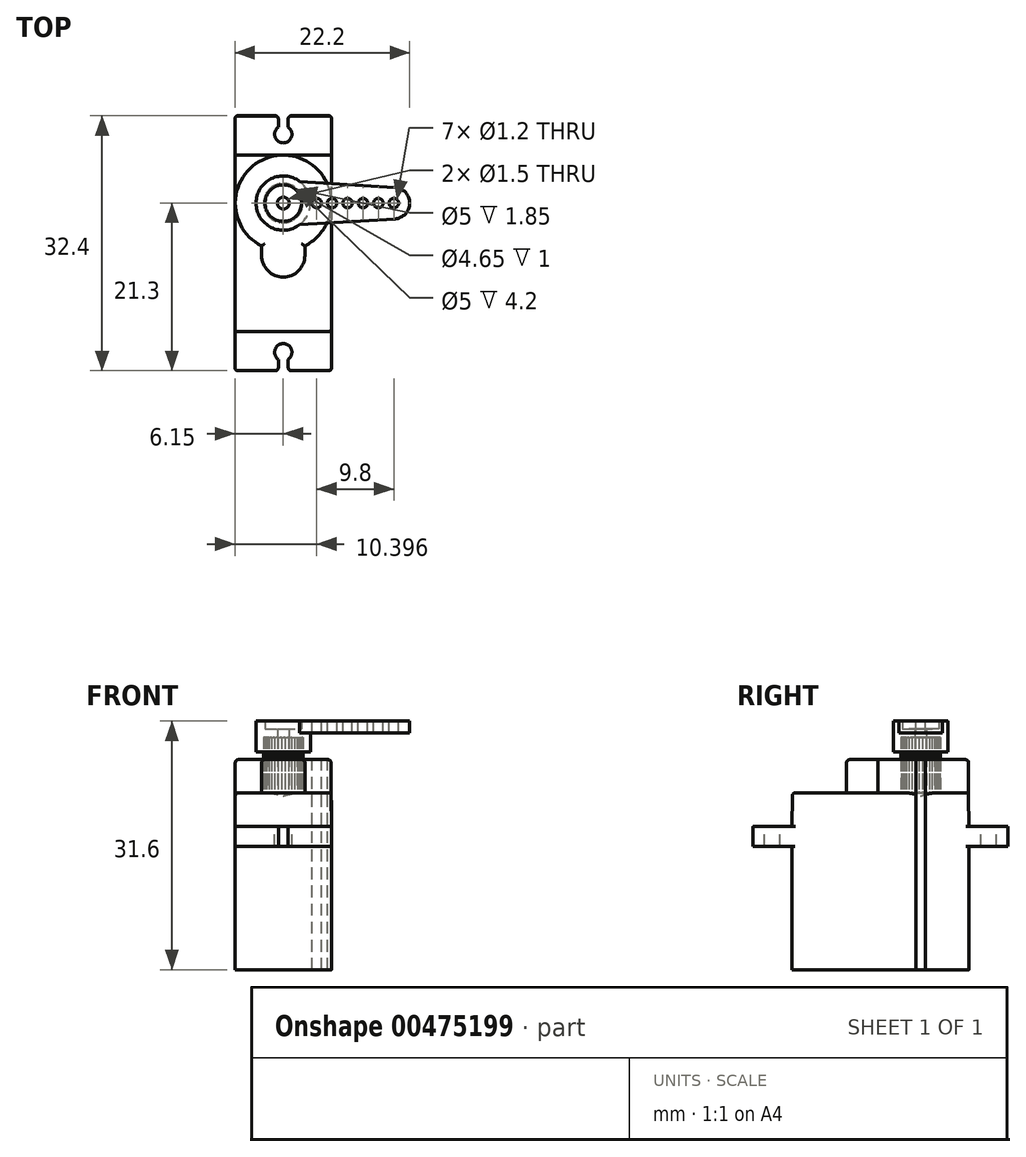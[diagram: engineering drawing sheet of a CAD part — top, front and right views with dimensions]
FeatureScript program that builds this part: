
annotation { "Feature Type Name" : "Feature", "Feature Type Description" : "" }
export const myFeature = defineFeature(function(context is Context, id is Id, definition is map)
    precondition{}
    {
        {
            var Q0;
            Q0=qCreatedBy(makeId("Top.planeOp"),FACE);
            var sketch = newSketch(context, id + "F0", { "sketchPlane" : qUnion([Q0])});
            skLineSegment(sketch, "E0.bottom", {"start": v(6.15, -11.25) * mm, "end": v(-6.15, -11.25) * mm});
            skLineSegment(sketch, "E0.top", {"start": v(6.15, 11.25) * mm, "end": v(-6.15, 11.25) * mm});
            skLineSegment(sketch, "E0.left", {"start": v(6.15, -11.25) * mm, "end": v(6.15, 11.25) * mm});
            skLineSegment(sketch, "E0.right", {"start": v(-6.15, -11.25) * mm, "end": v(-6.15, 11.25) * mm});
            skPoint(sketch, "E0.middle", {"position": v(0, 0) * mm});
            skSolve(sketch);
        }
        {
            var Q0;
            Q0=qSketchRegion(id+"F0",true);
            extrude(context, id + "F1", {"entities" : qUnion([Q0]), "depth" : (22.5 - 15.7) * mm, "hasDraft" : true, "draftAngle" : .5 * degree, "draftPullDirection" : true, "hasSecondDirection" : true, "secondDirectionOppositeDirection" : true, "secondDirectionDepth" : 15.7 * mm});
        }
        {
            var Q0;
            Q0=qCreatedBy(makeId("Top.planeOp"),FACE);
            var sketch = newSketch(context, id + "F2", { "sketchPlane" : qUnion([Q0])});
            skLineSegment(sketch, "E1.bottom", {"start": v(6.15, -16.2) * mm, "end": v(-6.15, -16.2) * mm});
            skLineSegment(sketch, "E1.top", {"start": v(6.15, 16.2) * mm, "end": v(-6.15, 16.2) * mm});
            skLineSegment(sketch, "E1.left", {"start": v(6.15, -16.2) * mm, "end": v(6.15, 16.2) * mm});
            skLineSegment(sketch, "E1.right", {"start": v(-6.15, -16.2) * mm, "end": v(-6.15, 16.2) * mm});
            skPoint(sketch, "E1.middle", {"position": v(0, 0) * mm});
            skSolve(sketch);
        }
        {
            var Q0;
            Q0=qSketchRegion(id+"F2",true);
            extrude(context, id + "F3", {"entities" : qUnion([Q0]), "operationType" : NewBodyOperationType.ADD, "depth" : 2.5 * mm, "hasDraft" : true, "draftAngle" : .5 * degree, "draftPullDirection" : true});
        }
        {
            var Q0;
            {var subQ0=sQuery(id+"F2.wireOp",EDGE,"E1.top");var subQ1=sQuery(id+"F2.wireOp",EDGE,"E1.right");var subQ2=sQuery(id+"F2.wireOp",EDGE,"E1.left");Q0=makeQuery(id+"F3.boolean.opBoolean","SPLIT",FACE,{"disambiguationData":[TD([makeQuery(id+"F1.opExtrude","SWEPT_FACE",FACE,{"disambiguationData":[OSD([sQuery(id+"F0.wireOp",EDGE,"E0.top")])]})])],"derivedFrom":makeQuery(id+"F3.opExtrude","CAP_FACE",FACE,{"disambiguationData":[OSD([sQuery(id+"F2.wireOp",EDGE,"E1.bottom"),subQ0,subQ2,subQ1])],"isStart":false})});}
            var sketch = newSketch(context, id + "F4", { "sketchPlane" : qUnion([Q0])});
            skArc(sketch, "E2", {"start": v(-0.63, 14.76) * mm, "mid": v(0, 12.75) * mm, "end": v(0.63, 14.76) * mm});
            skLineSegment(sketch, "E3", {"start": v(0, 0) * mm, "end": v(0, 13.85) * mm, "construction": true});
            skLineSegment(sketch, "E4", {"start": v(-0.63, 14.76) * mm, "end": v(-0.63, 16.2) * mm});
            skLineSegment(sketch, "E5", {"start": v(-0.62, 16.2) * mm, "end": v(0.62, 16.2) * mm});
            skLineSegment(sketch, "E6", {"start": v(0.62, 16.2) * mm, "end": v(0.62, 14.76) * mm});
            skLineSegment(sketch, "E7", {"start": v(0, 13.85) * mm, "end": v(0, 16.2) * mm, "construction": true});
            skLineSegment(sketch, "E8.MirrorCS", {"start": v(0.62, -16.2) * mm, "end": v(0.62, -14.76) * mm});
            skLineSegment(sketch, "E9.MirrorCS", {"start": v(-0.62, -16.2) * mm, "end": v(0.62, -16.2) * mm});
            skLineSegment(sketch, "E10.MirrorCS", {"start": v(-0.63, -14.76) * mm, "end": v(-0.63, -16.2) * mm});
            skArc(sketch, "E11.MirrorCS", {"start": v(-0.63, -14.76) * mm, "mid": v(0, -12.75) * mm, "end": v(0.63, -14.76) * mm});
            skSolve(sketch);
        }
        {
            var Q0;
            Q0=qSketchRegion(id+"F4",true);
            extrude(context, id + "F5", {"entities" : qUnion([Q0]), "operationType" : NewBodyOperationType.REMOVE, "endBound" : BoundingType.THROUGH_ALL, "oppositeDirection" : true, "depth" : 25 * mm});
        }
        {
            var Q0;
            Q0=makeQuery(id+"F1.*.split.splitOp","SPLIT",EDGE,{"derivedFrom":makeQuery(id+"F1.opExtrude","SWEPT_EDGE",EDGE,{"disambiguationData":[OSD([sQuery(id+"F0.wireOp",EDGE,"E0.bottom"),sQuery(id+"F0.wireOp",EDGE,"E0.left")])]})});
            var Q1;
            Q1=makeQuery(id+"F1.*.split.splitOp","SPLIT",EDGE,{"derivedFrom":makeQuery(id+"F1.opExtrude","SWEPT_EDGE",EDGE,{"disambiguationData":[OSD([sQuery(id+"F0.wireOp",EDGE,"E0.bottom"),sQuery(id+"F0.wireOp",EDGE,"E0.left")])]}),"isFromBackBody":true});
            var Q2;
            Q2=makeQuery(id+"F1.*.split.splitOp","SPLIT",EDGE,{"derivedFrom":makeQuery(id+"F1.opExtrude","SWEPT_EDGE",EDGE,{"disambiguationData":[OSD([sQuery(id+"F0.wireOp",EDGE,"E0.bottom"),sQuery(id+"F0.wireOp",EDGE,"E0.right")])]}),"isFromBackBody":true});
            var Q3;
            Q3=makeQuery(id+"F1.*.split.splitOp","SPLIT",EDGE,{"derivedFrom":makeQuery(id+"F1.opExtrude","SWEPT_EDGE",EDGE,{"disambiguationData":[OSD([sQuery(id+"F0.wireOp",EDGE,"E0.bottom"),sQuery(id+"F0.wireOp",EDGE,"E0.right")])]})});
            var Q4;
            Q4=makeQuery(id+"F1.opExtrude","CAP_FACE",FACE,{"disambiguationData":[OSD([sQuery(id+"F0.wireOp",EDGE,"E0.bottom"),sQuery(id+"F0.wireOp",EDGE,"E0.top"),sQuery(id+"F0.wireOp",EDGE,"E0.left"),sQuery(id+"F0.wireOp",EDGE,"E0.right")])],"isStart":false});
            var Q5;
            Q5=makeQuery(id+"F1.*.split.splitOp","SPLIT",EDGE,{"derivedFrom":makeQuery(id+"F1.opExtrude","SWEPT_EDGE",EDGE,{"disambiguationData":[OSD([sQuery(id+"F0.wireOp",EDGE,"E0.top"),sQuery(id+"F0.wireOp",EDGE,"E0.right")])]})});
            var Q6;
            Q6=makeQuery(id+"F1.*.split.splitOp","SPLIT",EDGE,{"derivedFrom":makeQuery(id+"F1.opExtrude","SWEPT_EDGE",EDGE,{"disambiguationData":[OSD([sQuery(id+"F0.wireOp",EDGE,"E0.top"),sQuery(id+"F0.wireOp",EDGE,"E0.right")])]}),"isFromBackBody":true});
            var Q7;
            Q7=makeQuery(id+"F1.*.split.splitOp","SPLIT",EDGE,{"derivedFrom":makeQuery(id+"F1.opExtrude","SWEPT_EDGE",EDGE,{"disambiguationData":[OSD([sQuery(id+"F0.wireOp",EDGE,"E0.top"),sQuery(id+"F0.wireOp",EDGE,"E0.left")])]}),"isFromBackBody":true});
            var Q8;
            Q8=makeQuery(id+"F1.*.split.splitOp","SPLIT",EDGE,{"derivedFrom":makeQuery(id+"F1.opExtrude","SWEPT_EDGE",EDGE,{"disambiguationData":[OSD([sQuery(id+"F0.wireOp",EDGE,"E0.top"),sQuery(id+"F0.wireOp",EDGE,"E0.left")])]})});
            var Q9;
            Q9=makeQuery(id+"F3.opExtrude","SWEPT_EDGE",EDGE,{"disambiguationData":[OSD([sQuery(id+"F2.wireOp",EDGE,"E1.top"),sQuery(id+"F2.wireOp",EDGE,"E1.left")])]});
            var Q10;
            Q10=makeQuery(id+"F5.boolean.opBoolean","INTERSECT",EDGE,{"derivedFrom":[makeQuery(id+"F3.opExtrude","SWEPT_FACE",FACE,{"disambiguationData":[OSD([sQuery(id+"F2.wireOp",EDGE,"E1.top")])]}),makeQuery(id+"F5.opExtrude","SWEPT_FACE",FACE,{"disambiguationData":[OSD([sQuery(id+"F4.wireOp",EDGE,"E6")])]})]});
            var Q11;
            Q11=makeQuery(id+"F5.boolean.opBoolean","INTERSECT",EDGE,{"derivedFrom":[makeQuery(id+"F3.opExtrude","SWEPT_FACE",FACE,{"disambiguationData":[OSD([sQuery(id+"F2.wireOp",EDGE,"E1.top")])]}),makeQuery(id+"F5.opExtrude","SWEPT_FACE",FACE,{"disambiguationData":[OSD([sQuery(id+"F4.wireOp",EDGE,"E4")])]})]});
            var Q12;
            Q12=makeQuery(id+"F3.opExtrude","SWEPT_EDGE",EDGE,{"disambiguationData":[OSD([sQuery(id+"F2.wireOp",EDGE,"E1.top"),sQuery(id+"F2.wireOp",EDGE,"E1.right")])]});
            var Q13;
            Q13=makeQuery(id+"F3.opExtrude","SWEPT_EDGE",EDGE,{"disambiguationData":[OSD([sQuery(id+"F2.wireOp",EDGE,"E1.bottom"),sQuery(id+"F2.wireOp",EDGE,"E1.right")])]});
            var Q14;
            Q14=makeQuery(id+"F5.boolean.opBoolean","INTERSECT",EDGE,{"derivedFrom":[makeQuery(id+"F3.opExtrude","SWEPT_FACE",FACE,{"disambiguationData":[OSD([sQuery(id+"F2.wireOp",EDGE,"E1.bottom")])]}),makeQuery(id+"F5.opExtrude","SWEPT_FACE",FACE,{"disambiguationData":[OSD([sQuery(id+"F4.wireOp",EDGE,"E10.MirrorCS")])]})]});
            var Q15;
            Q15=makeQuery(id+"F5.boolean.opBoolean","INTERSECT",EDGE,{"derivedFrom":[makeQuery(id+"F3.opExtrude","SWEPT_FACE",FACE,{"disambiguationData":[OSD([sQuery(id+"F2.wireOp",EDGE,"E1.bottom")])]}),makeQuery(id+"F5.opExtrude","SWEPT_FACE",FACE,{"disambiguationData":[OSD([sQuery(id+"F4.wireOp",EDGE,"E8.MirrorCS")])]})]});
            var Q16;
            Q16=makeQuery(id+"F3.opExtrude","SWEPT_EDGE",EDGE,{"disambiguationData":[OSD([sQuery(id+"F2.wireOp",EDGE,"E1.bottom"),sQuery(id+"F2.wireOp",EDGE,"E1.left")])]});
            fillet(context, id + "F6", {"entities" : qUnion([Q0, Q1, Q2, Q3, Q4, Q5, Q6, Q7, Q8, Q9, Q10, Q11, Q12, Q13, Q14, Q15, Q16]), "radius" : .4 * mm, "tangentPropagation" : true, "allowEdgeOverflow" : false});
        }
        {
            var Q0;
            Q0=makeQuery(id+"F1.opExtrude","CAP_FACE",FACE,{"disambiguationData":[OSD([sQuery(id+"F0.wireOp",EDGE,"E0.bottom"),sQuery(id+"F0.wireOp",EDGE,"E0.top"),sQuery(id+"F0.wireOp",EDGE,"E0.left"),sQuery(id+"F0.wireOp",EDGE,"E0.right")])],"isStart":false});
            var sketch = newSketch(context, id + "F7", { "sketchPlane" : qUnion([Q0])});
            skArc(sketch, "E12", {"start": v(2.75, -0.34) * mm, "mid": v(0, 11.2) * mm, "end": v(-2.75, -0.34) * mm});
            skLineSegment(sketch, "E13", {"start": v(-2.75, -0.34) * mm, "end": v(-2.75, -1.56) * mm});
            skLineSegment(sketch, "E14", {"start": v(2.75, -0.34) * mm, "end": v(2.75, -1.56) * mm});
            skArc(sketch, "E15", {"start": v(-2.75, -1.56) * mm, "mid": v(0, -4.3) * mm, "end": v(2.75, -1.56) * mm});
            skCircle(sketch, "E16", {"center": v(0, 5.1) * mm, "radius": 2.5 * mm});
            skSolve(sketch);
        }
        {
            var Q0;
            Q0=qSketchRegion(id+"F7",true);
            extrude(context, id + "F8", {"entities" : qUnion([Q0]), "operationType" : NewBodyOperationType.ADD, "depth" : 4.2 * mm, "hasSecondDirection" : true, "secondDirectionBound" : SecondDirectionBoundingType.UP_TO_NEXT, "secondDirectionOppositeDirection" : true, "secondDirectionDepth" : 25 * mm});
        }
        {
            var Q0;
            Q0=makeQuery(id+"F8.opExtrude","CAP_EDGE",EDGE,{"disambiguationData":[OSD([sQuery(id+"F7.wireOp",EDGE,"E12")])],"isStart":false});
            var Q1;
            Q1=makeQuery(id+"F8.opExtrude","CAP_EDGE",EDGE,{"disambiguationData":[OSD([sQuery(id+"F7.wireOp",EDGE,"E14")])],"isStart":false});
            var Q2;
            Q2=makeQuery(id+"F8.opExtrude","CAP_EDGE",EDGE,{"disambiguationData":[OSD([sQuery(id+"F7.wireOp",EDGE,"E15")])],"isStart":false});
            var Q3;
            Q3=makeQuery(id+"F8.opExtrude","CAP_EDGE",EDGE,{"disambiguationData":[OSD([sQuery(id+"F7.wireOp",EDGE,"E13")])],"isStart":false});
            fillet(context, id + "F9", {"entities" : qUnion([Q0, Q1, Q2, Q3]), "radius" : .4 * mm, "tangentPropagation" : true, "allowEdgeOverflow" : false});
        }
        {
            var Q0;
            Q0=makeQuery(id+"F8.opExtrude","CAP_FACE",FACE,{"disambiguationData":[OSD([sQuery(id+"F7.wireOp",EDGE,"E12"),sQuery(id+"F7.wireOp",EDGE,"E13"),sQuery(id+"F7.wireOp",EDGE,"E14"),sQuery(id+"F7.wireOp",EDGE,"E15"),sQuery(id+"F7.wireOp",EDGE,"E16")])],"isStart":false});
            var sketch = newSketch(context, id + "F10", { "sketchPlane" : qUnion([Q0])});
            skCircle(sketch, "E17", {"center": v(0, 5.1) * mm, "radius": 2.3 * mm, "construction": true});
            skLineSegment(sketch, "E18", {"start": v(-0.23, 7.39) * mm, "end": v(-0.06, 7.57) * mm});
            skLineSegment(sketch, "E19", {"start": v(0.23, 7.39) * mm, "end": v(0.06, 7.57) * mm});
            skArc(sketch, "E20", {"start": v(0.06, 7.57) * mm, "mid": v(0, 7.6) * mm, "end": v(-0.06, 7.57) * mm});
            skLineSegment(sketch, "E21", {"start": v(-0.23, 7.39) * mm, "end": v(0, 5.1) * mm, "construction": true});
            skLineSegment(sketch, "E22", {"start": v(0.23, 7.39) * mm, "end": v(0, 5.1) * mm, "construction": true});
            skLineSegment(sketch, "E23.1.0", {"start": v(-0.67, 7.3) * mm, "end": v(-0.54, 7.51) * mm});
            skArc(sketch, "E23.1.1", {"start": v(-0.42, 7.54) * mm, "mid": v(-0.49, 7.55) * mm, "end": v(-0.54, 7.51) * mm});
            skLineSegment(sketch, "E23.1.2", {"start": v(-0.23, 7.39) * mm, "end": v(-0.42, 7.54) * mm});
            skLineSegment(sketch, "E23.2.0", {"start": v(-1.08, 7.13) * mm, "end": v(-1, 7.36) * mm});
            skArc(sketch, "E23.2.1", {"start": v(-0.9, 7.4) * mm, "mid": v(-0.96, 7.4) * mm, "end": v(-1, 7.36) * mm});
            skLineSegment(sketch, "E23.2.2", {"start": v(-0.67, 7.3) * mm, "end": v(-0.9, 7.4) * mm});
            skLineSegment(sketch, "E23.3.0", {"start": v(-1.46, 6.88) * mm, "end": v(-1.42, 7.12) * mm});
            skArc(sketch, "E23.3.1", {"start": v(-1.32, 7.19) * mm, "mid": v(-1.39, 7.18) * mm, "end": v(-1.42, 7.12) * mm});
            skLineSegment(sketch, "E23.3.2", {"start": v(-1.08, 7.13) * mm, "end": v(-1.32, 7.19) * mm});
            skLineSegment(sketch, "E23.4.0", {"start": v(-1.78, 6.56) * mm, "end": v(-1.8, 6.8) * mm});
            skArc(sketch, "E23.4.1", {"start": v(-1.7, 6.9) * mm, "mid": v(-1.77, 6.87) * mm, "end": v(-1.8, 6.8) * mm});
            skLineSegment(sketch, "E23.4.2", {"start": v(-1.46, 6.88) * mm, "end": v(-1.7, 6.9) * mm});
            skLineSegment(sketch, "E23.5.0", {"start": v(-2.03, 6.18) * mm, "end": v(-2.09, 6.42) * mm});
            skArc(sketch, "E23.5.1", {"start": v(-2.02, 6.52) * mm, "mid": v(-2.08, 6.49) * mm, "end": v(-2.09, 6.42) * mm});
            skLineSegment(sketch, "E23.5.2", {"start": v(-1.78, 6.56) * mm, "end": v(-2.02, 6.52) * mm});
            skLineSegment(sketch, "E23.6.0", {"start": v(-2.2, 5.77) * mm, "end": v(-2.3, 6) * mm});
            skArc(sketch, "E23.6.1", {"start": v(-2.26, 6.1) * mm, "mid": v(-2.3, 6.06) * mm, "end": v(-2.3, 6) * mm});
            skLineSegment(sketch, "E23.6.2", {"start": v(-2.03, 6.18) * mm, "end": v(-2.26, 6.1) * mm});
            skLineSegment(sketch, "E23.7.0", {"start": v(-2.29, 5.33) * mm, "end": v(-2.44, 5.52) * mm});
            skArc(sketch, "E23.7.1", {"start": v(-2.41, 5.64) * mm, "mid": v(-2.45, 5.59) * mm, "end": v(-2.44, 5.52) * mm});
            skLineSegment(sketch, "E23.7.2", {"start": v(-2.2, 5.77) * mm, "end": v(-2.41, 5.64) * mm});
            skLineSegment(sketch, "E23.8.0", {"start": v(-2.29, 4.87) * mm, "end": v(-2.47, 5.04) * mm});
            skArc(sketch, "E23.8.1", {"start": v(-2.47, 5.16) * mm, "mid": v(-2.5, 5.1) * mm, "end": v(-2.47, 5.04) * mm});
            skLineSegment(sketch, "E23.8.2", {"start": v(-2.29, 5.33) * mm, "end": v(-2.47, 5.16) * mm});
            skLineSegment(sketch, "E23.9.0", {"start": v(-2.2, 4.43) * mm, "end": v(-2.41, 4.56) * mm});
            skArc(sketch, "E23.9.1", {"start": v(-2.44, 4.68) * mm, "mid": v(-2.45, 4.61) * mm, "end": v(-2.41, 4.56) * mm});
            skLineSegment(sketch, "E23.9.2", {"start": v(-2.29, 4.87) * mm, "end": v(-2.44, 4.68) * mm});
            skLineSegment(sketch, "E23.10.0", {"start": v(-2.03, 4.02) * mm, "end": v(-2.26, 4.1) * mm});
            skArc(sketch, "E23.10.1", {"start": v(-2.3, 4.2) * mm, "mid": v(-2.3, 4.14) * mm, "end": v(-2.26, 4.1) * mm});
            skLineSegment(sketch, "E23.10.2", {"start": v(-2.2, 4.43) * mm, "end": v(-2.3, 4.2) * mm});
            skLineSegment(sketch, "E23.11.0", {"start": v(-1.78, 3.64) * mm, "end": v(-2.02, 3.68) * mm});
            skArc(sketch, "E23.11.1", {"start": v(-2.09, 3.78) * mm, "mid": v(-2.08, 3.71) * mm, "end": v(-2.02, 3.68) * mm});
            skLineSegment(sketch, "E23.11.2", {"start": v(-2.03, 4.02) * mm, "end": v(-2.09, 3.78) * mm});
            skLineSegment(sketch, "E23.12.0", {"start": v(-1.46, 3.32) * mm, "end": v(-1.7, 3.3) * mm});
            skArc(sketch, "E23.12.1", {"start": v(-1.8, 3.4) * mm, "mid": v(-1.77, 3.33) * mm, "end": v(-1.7, 3.3) * mm});
            skLineSegment(sketch, "E23.12.2", {"start": v(-1.78, 3.64) * mm, "end": v(-1.8, 3.4) * mm});
            skLineSegment(sketch, "E23.13.0", {"start": v(-1.08, 3.07) * mm, "end": v(-1.32, 3.01) * mm});
            skArc(sketch, "E23.13.1", {"start": v(-1.42, 3.08) * mm, "mid": v(-1.39, 3.02) * mm, "end": v(-1.32, 3.01) * mm});
            skLineSegment(sketch, "E23.13.2", {"start": v(-1.46, 3.32) * mm, "end": v(-1.42, 3.08) * mm});
            skLineSegment(sketch, "E23.14.0", {"start": v(-0.67, 2.9) * mm, "end": v(-0.9, 2.8) * mm});
            skArc(sketch, "E23.14.1", {"start": v(-1, 2.84) * mm, "mid": v(-0.96, 2.8) * mm, "end": v(-0.9, 2.8) * mm});
            skLineSegment(sketch, "E23.14.2", {"start": v(-1.08, 3.07) * mm, "end": v(-1, 2.84) * mm});
            skLineSegment(sketch, "E23.15.0", {"start": v(-0.23, 2.81) * mm, "end": v(-0.42, 2.66) * mm});
            skArc(sketch, "E23.15.1", {"start": v(-0.54, 2.69) * mm, "mid": v(-0.49, 2.65) * mm, "end": v(-0.42, 2.66) * mm});
            skLineSegment(sketch, "E23.15.2", {"start": v(-0.67, 2.9) * mm, "end": v(-0.54, 2.69) * mm});
            skLineSegment(sketch, "E23.16.0", {"start": v(0.23, 2.81) * mm, "end": v(0.06, 2.63) * mm});
            skArc(sketch, "E23.16.1", {"start": v(-0.06, 2.63) * mm, "mid": v(0, 2.6) * mm, "end": v(0.06, 2.63) * mm});
            skLineSegment(sketch, "E23.16.2", {"start": v(-0.23, 2.81) * mm, "end": v(-0.06, 2.63) * mm});
            skLineSegment(sketch, "E23.17.0", {"start": v(0.67, 2.9) * mm, "end": v(0.54, 2.69) * mm});
            skArc(sketch, "E23.17.1", {"start": v(0.42, 2.66) * mm, "mid": v(0.49, 2.65) * mm, "end": v(0.54, 2.69) * mm});
            skLineSegment(sketch, "E23.17.2", {"start": v(0.23, 2.81) * mm, "end": v(0.42, 2.66) * mm});
            skLineSegment(sketch, "E23.18.0", {"start": v(1.08, 3.07) * mm, "end": v(1, 2.84) * mm});
            skArc(sketch, "E23.18.1", {"start": v(0.9, 2.8) * mm, "mid": v(0.96, 2.8) * mm, "end": v(1, 2.84) * mm});
            skLineSegment(sketch, "E23.18.2", {"start": v(0.67, 2.9) * mm, "end": v(0.9, 2.8) * mm});
            skLineSegment(sketch, "E23.19.0", {"start": v(1.46, 3.32) * mm, "end": v(1.42, 3.08) * mm});
            skArc(sketch, "E23.19.1", {"start": v(1.32, 3.01) * mm, "mid": v(1.39, 3.02) * mm, "end": v(1.42, 3.08) * mm});
            skLineSegment(sketch, "E23.19.2", {"start": v(1.08, 3.07) * mm, "end": v(1.32, 3.01) * mm});
            skLineSegment(sketch, "E23.20.0", {"start": v(1.78, 3.64) * mm, "end": v(1.8, 3.4) * mm});
            skArc(sketch, "E23.20.1", {"start": v(1.7, 3.3) * mm, "mid": v(1.77, 3.33) * mm, "end": v(1.8, 3.4) * mm});
            skLineSegment(sketch, "E23.20.2", {"start": v(1.46, 3.32) * mm, "end": v(1.7, 3.3) * mm});
            skLineSegment(sketch, "E23.21.0", {"start": v(2.03, 4.02) * mm, "end": v(2.09, 3.78) * mm});
            skArc(sketch, "E23.21.1", {"start": v(2.02, 3.68) * mm, "mid": v(2.08, 3.71) * mm, "end": v(2.09, 3.78) * mm});
            skLineSegment(sketch, "E23.21.2", {"start": v(1.78, 3.64) * mm, "end": v(2.02, 3.68) * mm});
            skLineSegment(sketch, "E23.22.0", {"start": v(2.2, 4.43) * mm, "end": v(2.3, 4.2) * mm});
            skArc(sketch, "E23.22.1", {"start": v(2.26, 4.1) * mm, "mid": v(2.3, 4.14) * mm, "end": v(2.3, 4.2) * mm});
            skLineSegment(sketch, "E23.22.2", {"start": v(2.03, 4.02) * mm, "end": v(2.26, 4.1) * mm});
            skLineSegment(sketch, "E23.23.0", {"start": v(2.29, 4.87) * mm, "end": v(2.44, 4.68) * mm});
            skArc(sketch, "E23.23.1", {"start": v(2.41, 4.56) * mm, "mid": v(2.45, 4.61) * mm, "end": v(2.44, 4.68) * mm});
            skLineSegment(sketch, "E23.23.2", {"start": v(2.2, 4.43) * mm, "end": v(2.41, 4.56) * mm});
            skLineSegment(sketch, "E23.24.0", {"start": v(2.29, 5.33) * mm, "end": v(2.47, 5.16) * mm});
            skArc(sketch, "E23.24.1", {"start": v(2.47, 5.04) * mm, "mid": v(2.5, 5.1) * mm, "end": v(2.47, 5.16) * mm});
            skLineSegment(sketch, "E23.24.2", {"start": v(2.29, 4.87) * mm, "end": v(2.47, 5.04) * mm});
            skLineSegment(sketch, "E23.25.0", {"start": v(2.2, 5.77) * mm, "end": v(2.41, 5.64) * mm});
            skArc(sketch, "E23.25.1", {"start": v(2.44, 5.52) * mm, "mid": v(2.45, 5.59) * mm, "end": v(2.41, 5.64) * mm});
            skLineSegment(sketch, "E23.25.2", {"start": v(2.29, 5.33) * mm, "end": v(2.44, 5.52) * mm});
            skLineSegment(sketch, "E23.26.0", {"start": v(2.03, 6.18) * mm, "end": v(2.26, 6.1) * mm});
            skArc(sketch, "E23.26.1", {"start": v(2.3, 6) * mm, "mid": v(2.3, 6.06) * mm, "end": v(2.26, 6.1) * mm});
            skLineSegment(sketch, "E23.26.2", {"start": v(2.2, 5.77) * mm, "end": v(2.3, 6) * mm});
            skLineSegment(sketch, "E23.27.0", {"start": v(1.78, 6.56) * mm, "end": v(2.02, 6.52) * mm});
            skArc(sketch, "E23.27.1", {"start": v(2.09, 6.42) * mm, "mid": v(2.08, 6.49) * mm, "end": v(2.02, 6.52) * mm});
            skLineSegment(sketch, "E23.27.2", {"start": v(2.03, 6.18) * mm, "end": v(2.09, 6.42) * mm});
            skLineSegment(sketch, "E23.28.0", {"start": v(1.46, 6.88) * mm, "end": v(1.7, 6.9) * mm});
            skArc(sketch, "E23.28.1", {"start": v(1.8, 6.8) * mm, "mid": v(1.77, 6.87) * mm, "end": v(1.7, 6.9) * mm});
            skLineSegment(sketch, "E23.28.2", {"start": v(1.78, 6.56) * mm, "end": v(1.8, 6.8) * mm});
            skLineSegment(sketch, "E23.29.0", {"start": v(1.08, 7.13) * mm, "end": v(1.32, 7.19) * mm});
            skArc(sketch, "E23.29.1", {"start": v(1.42, 7.12) * mm, "mid": v(1.39, 7.18) * mm, "end": v(1.32, 7.19) * mm});
            skLineSegment(sketch, "E23.29.2", {"start": v(1.46, 6.88) * mm, "end": v(1.42, 7.12) * mm});
            skLineSegment(sketch, "E23.30.0", {"start": v(0.67, 7.3) * mm, "end": v(0.9, 7.4) * mm});
            skArc(sketch, "E23.30.1", {"start": v(1, 7.36) * mm, "mid": v(0.96, 7.4) * mm, "end": v(0.9, 7.4) * mm});
            skLineSegment(sketch, "E23.30.2", {"start": v(1.08, 7.13) * mm, "end": v(1, 7.36) * mm});
            skLineSegment(sketch, "E23.31.0", {"start": v(0.23, 7.39) * mm, "end": v(0.42, 7.54) * mm});
            skArc(sketch, "E23.31.1", {"start": v(0.54, 7.51) * mm, "mid": v(0.49, 7.55) * mm, "end": v(0.42, 7.54) * mm});
            skLineSegment(sketch, "E23.31.2", {"start": v(0.67, 7.3) * mm, "end": v(0.54, 7.51) * mm});
            skCircle(sketch, "E24", {"center": v(0, 5.1) * mm, "radius": 0.75 * mm});
            skSolve(sketch);
        }
        {
            var Q0;
            Q0=qSketchRegion(id+"F10",true);
            extrude(context, id + "F11", {"entities" : qUnion([Q0]), "depth" : 2.85 * mm, "hasSecondDirection" : true, "secondDirectionBound" : SecondDirectionBoundingType.UP_TO_NEXT, "secondDirectionOppositeDirection" : true, "secondDirectionDepth" : 25 * mm});
        }
        {
            var Q0;
            Q0=qCreatedBy(makeId("Right.planeOp"),FACE);
            var sketch = newSketch(context, id + "F12", { "sketchPlane" : qUnion([Q0])});
            skLineSegment(sketch, "E25.0", {"start": v(4.35, 13.85) * mm, "end": v(5.85, 13.85) * mm, "construction": true});
            skLineSegment(sketch, "E26", {"start": v(5.85, 13.85) * mm, "end": v(7.6, 13.85) * mm});
            skLineSegment(sketch, "E27", {"start": v(7.6, 13.85) * mm, "end": v(7.6, 12) * mm});
            skLineSegment(sketch, "E28", {"start": v(7.6, 12) * mm, "end": v(8.55, 12) * mm});
            skLineSegment(sketch, "E29", {"start": v(8.55, 12) * mm, "end": v(8.55, 15.9) * mm});
            skLineSegment(sketch, "E30", {"start": v(8.55, 15.9) * mm, "end": v(7.43, 15.9) * mm});
            skLineSegment(sketch, "E31", {"start": v(7.43, 15.9) * mm, "end": v(7.43, 14.9) * mm});
            skLineSegment(sketch, "E32", {"start": v(7.43, 14.9) * mm, "end": v(5.85, 14.9) * mm});
            skLineSegment(sketch, "E33", {"start": v(5.85, 14.9) * mm, "end": v(5.85, 13.85) * mm});
            skLineSegment(sketch, "E34", {"start": v(5.1, 13.85) * mm, "end": v(5.1, 16.3) * mm, "construction": true});
            skLineSegment(sketch, "E35.0", {"start": v(2.6, 11) * mm, "end": v(7.6, 11) * mm, "construction": true});
            skSolve(sketch);
        }
        {
            var Q0;
            Q0=qSketchRegion(id+"F12",true);
            var Q1;
            Q1=sQuery(id+"F12.wireOp",EDGE,"E34");
            revolve(context, id + "F13", {"entities" : qUnion([Q0]), "axis" : qUnion([Q1]), "revolveType" : RevolveType.FULL});
        }
        {
            var Q0;
            Q0=makeQuery(id+"F13.opRevolve","SWEPT_FACE",FACE,{"disambiguationData":[OSD([sQuery(id+"F12.wireOp",EDGE,"E30")])]});
            var sketch = newSketch(context, id + "F14", { "sketchPlane" : qUnion([Q0])});
            skLineSegment(sketch, "E36", {"start": v(2.08, 2.35) * mm, "end": v(14.17, 3.1) * mm});
            skLineSegment(sketch, "E37", {"start": v(2.08, 7.85) * mm, "end": v(14.17, 7.1) * mm});
            skLineSegment(sketch, "E38", {"start": v(0, 5.1) * mm, "end": v(14.05, 5.1) * mm, "construction": true});
            skArc(sketch, "E39", {"start": v(14.17, 3.1) * mm, "mid": v(16.05, 5.1) * mm, "end": v(14.17, 7.1) * mm});
            skArc(sketch, "E40.0", {"start": v(2.08, 2.35) * mm, "mid": v(3.45, 5.1) * mm, "end": v(2.08, 7.85) * mm});
            skSolve(sketch);
        }
        {
            var Q0;
            Q0=qSketchRegion(id+"F14",true);
            extrude(context, id + "F15", {"entities" : qUnion([Q0]), "operationType" : NewBodyOperationType.ADD, "oppositeDirection" : true, "depth" : 1.5 * mm});
        }
        {
            var Q0;
            Q0=makeQuery(id+"F15.boolean.opBoolean","MERGE",FACE,{"derivedFrom":[makeQuery(id+"F13.opRevolve","SWEPT_FACE",FACE,{"disambiguationData":[OSD([sQuery(id+"F12.wireOp",EDGE,"E30")])]}),makeQuery(id+"F15.opExtrude","CAP_FACE",FACE,{"disambiguationData":[OSD([sQuery(id+"F14.wireOp",EDGE,"E36"),sQuery(id+"F14.wireOp",EDGE,"E37"),sQuery(id+"F14.wireOp",EDGE,"E39"),sQuery(id+"F14.wireOp",EDGE,"E40.0")])],"isStart":true})]});
            var sketch = newSketch(context, id + "F16", { "sketchPlane" : qUnion([Q0])});
            skCircle(sketch, "E41", {"center": v(14.05, 5.1) * mm, "radius": 0.6 * mm});
            skCircle(sketch, "E42.1.0.0", {"center": v(12.09, 5.1) * mm, "radius": 0.6 * mm});
            skCircle(sketch, "E42.2.0.0", {"center": v(10.13, 5.1) * mm, "radius": 0.6 * mm});
            skCircle(sketch, "E42.3.0.0", {"center": v(8.17, 5.1) * mm, "radius": 0.6 * mm});
            skCircle(sketch, "E42.4.0.0", {"center": v(6.2, 5.1) * mm, "radius": 0.6 * mm});
            skCircle(sketch, "E42.5.0.0", {"center": v(4.25, 5.1) * mm, "radius": 0.6 * mm});
            skLineSegment(sketch, "E42.direction1", {"start": v(14.05, 5.1) * mm, "end": v(12.09, 5.1) * mm, "construction": true});
            skSolve(sketch);
        }
        {
            var Q0;
            Q0=qSketchRegion(id+"F16",true);
            extrude(context, id + "F17", {"entities" : qUnion([Q0]), "operationType" : NewBodyOperationType.REMOVE, "endBound" : BoundingType.THROUGH_ALL, "oppositeDirection" : true, "depth" : 25 * mm});
        }
    });
